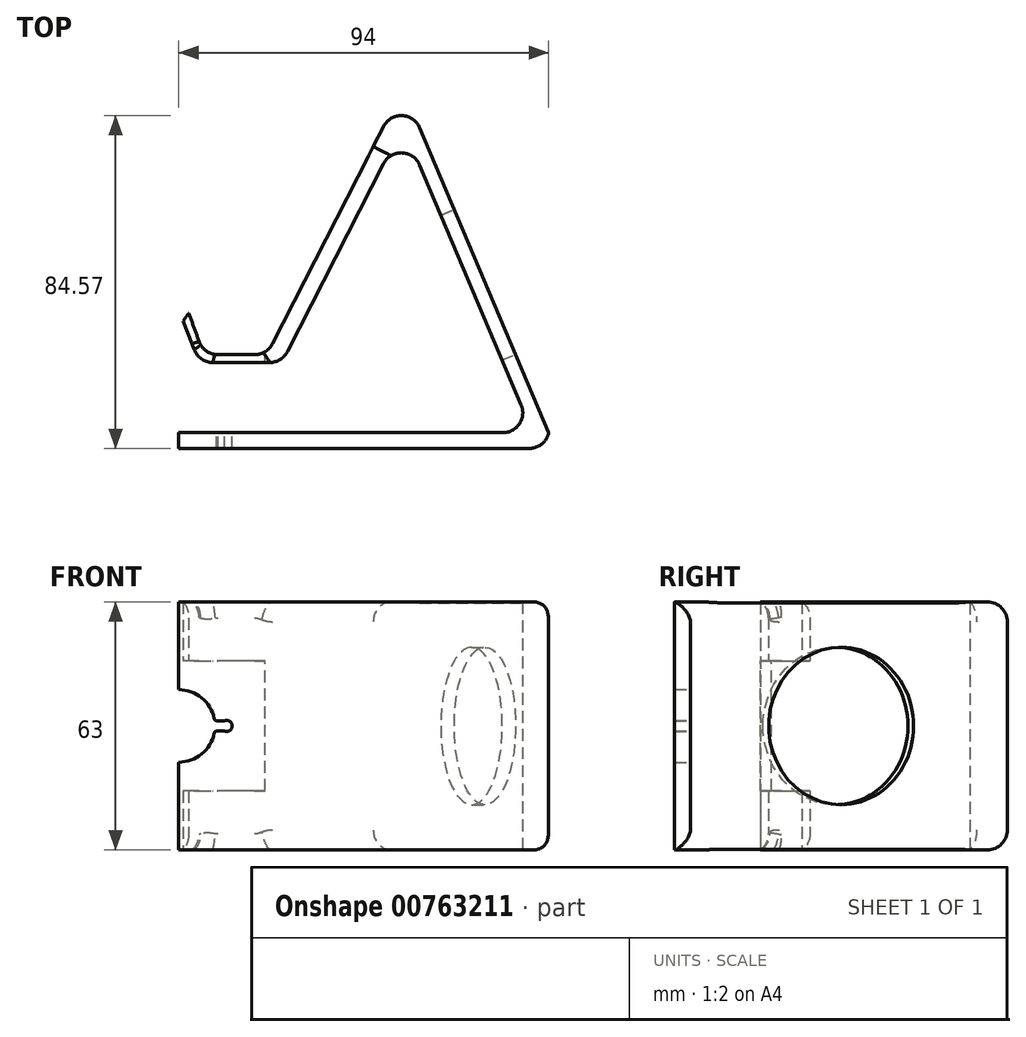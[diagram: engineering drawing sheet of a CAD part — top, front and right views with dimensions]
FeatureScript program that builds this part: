
annotation { "Feature Type Name" : "Feature", "Feature Type Description" : "" }
export const myFeature = defineFeature(function(context is Context, id is Id, definition is map)
    precondition{}
    {
        {
            var Q0;
            Q0=qCreatedBy(makeId("Top.planeOp"),FACE);
            var sketch = newSketch(context, id + "F0", { "sketchPlane" : qUnion([Q0])});
            skLineSegment(sketch, "E0", {"start": v(0, 43.75) * mm, "end": v(0, -43.75) * mm, "construction": true});
            skLineSegment(sketch, "E1", {"start": v(-37, -43.75) * mm, "end": v(33, -43.75) * mm});
            skPoint(sketch, "E2", {"position": v(0, -43.75) * mm});
            skLineSegment(sketch, "E3", {"start": v(0, 43.75) * mm, "end": v(37, -43.75) * mm});
            skLineSegment(sketch, "E4", {"start": v(0, 43.75) * mm, "end": v(-34.6, -23.92) * mm});
            skLineSegment(sketch, "E5.top", {"start": v(-37, -47.75) * mm, "end": v(37, -47.75) * mm});
            skLineSegment(sketch, "E5.right", {"start": v(37, -43.75) * mm, "end": v(37, -47.75) * mm});
            skLineSegment(sketch, "E6", {"start": v(33, -43.75) * mm, "end": v(0, 34.3) * mm});
            skLineSegment(sketch, "E7", {"start": v(0, 34.3) * mm, "end": v(-30.78, -25.92) * mm});
            skLineSegment(sketch, "E8", {"start": v(-30.78, -25.92) * mm, "end": v(-51.78, -25.92) * mm});
            skLineSegment(sketch, "E9", {"start": v(-51.78, -25.92) * mm, "end": v(-55.84, -15.4) * mm});
            skLineSegment(sketch, "E10", {"start": v(-34.6, -23.92) * mm, "end": v(-50.6, -23.92) * mm});
            skLineSegment(sketch, "E11", {"start": v(-50.6, -23.92) * mm, "end": v(-54.45, -13.32) * mm});
            skLineSegment(sketch, "E12", {"start": v(-54.45, -13.32) * mm, "end": v(-55.84, -15.4) * mm});
            skLineSegment(sketch, "E13", {"start": v(-55.84, -15.4) * mm, "end": v(0, -15.4) * mm, "construction": true});
            skLineSegment(sketch, "E14", {"start": v(-55.84, -15.4) * mm, "end": v(-55.84, 0) * mm, "construction": true});
            skLineSegment(sketch, "E15.bottom", {"start": v(-37, -47.75) * mm, "end": v(-57, -47.75) * mm});
            skLineSegment(sketch, "E15.top", {"start": v(-37, -43.75) * mm, "end": v(-57, -43.75) * mm});
            skLineSegment(sketch, "E15.right", {"start": v(-57, -47.75) * mm, "end": v(-57, -43.75) * mm});
            skSolve(sketch);
        }
        {
            var Q0;
            Q0 = qSketchRegion(id + "F0", true);
            extrude(context, id + "F1", {"entities" : qUnion([Q0]), "depth" : 63 * mm, "offsetDistance" : 25.4 * mm});
        }
        {
            var Q0;
            Q0=qCreatedBy(makeId("Right.planeOp"),FACE);
            cPlane(context, id + "F2", {"entities" : qUnion([Q0]), "cplaneType" : CPlaneType.OFFSET, "offset" : 56 * mm, "oppositeDirection" : true, "width" : 152.4 * mm, "height" : 152.4 * mm});
        }
        {
            var Q0;
            Q0=qCreatedBy(id+"F2.planeOp",FACE);
            var sketch = newSketch(context, id + "F3", { "sketchPlane" : qUnion([Q0])});
            skLineSegment(sketch, "E16", {"start": v(0, 0) * mm, "end": v(-30, 0) * mm, "construction": true});
            skLineSegment(sketch, "E17", {"start": v(-30, 0) * mm, "end": v(-30, 63) * mm, "construction": true});
            skPoint(sketch, "E18", {"position": v(-30, 15) * mm});
            skPoint(sketch, "E19", {"position": v(-30, 48) * mm});
            skLineSegment(sketch, "E20.bottom", {"start": v(-30, 15) * mm, "end": v(-6.4, 15) * mm});
            skLineSegment(sketch, "E20.top", {"start": v(-30, 48) * mm, "end": v(-6.4, 48) * mm});
            skLineSegment(sketch, "E20.left", {"start": v(-30, 15) * mm, "end": v(-30, 48) * mm});
            skLineSegment(sketch, "E20.right", {"start": v(-6.4, 15) * mm, "end": v(-6.4, 48) * mm});
            skSolve(sketch);
        }
        {
            var Q0;
            Q0=makeQuery(id+"F3.imprint","IMPRINT",FACE,{"disambiguationData":[TD([[makeQuery(id+"F3.imprint","IMPRINT",EDGE,{"derivedFrom":sQuery(id+"F3.wireOp",EDGE,"E20.bottom")}),1.0]])]});
            extrude(context, id + "F4", {"entities" : qUnion([Q0]), "operationType" : NewBodyOperationType.REMOVE, "depth" : 21 * mm, "offsetDistance" : 25.4 * mm});
        }
        {
            var Q0;
            Q0=makeQuery(id+"F1.opExtrude","SWEPT_EDGE",EDGE,{"disambiguationData":[OSD([sQuery(id+"F0.wireOp",EDGE,"E3"),sQuery(id+"F0.wireOp",EDGE,"E4")])]});
            var Q1;
            Q1=makeQuery(id+"F1.opExtrude","SWEPT_EDGE",EDGE,{"disambiguationData":[OSD([sQuery(id+"F0.wireOp",EDGE,"E6"),sQuery(id+"F0.wireOp",EDGE,"E7")])]});
            var Q2;
            Q2=makeQuery(id+"F1.opExtrude","SWEPT_EDGE",EDGE,{"disambiguationData":[OSD([sQuery(id+"F0.wireOp",EDGE,"E1"),sQuery(id+"F0.wireOp",EDGE,"E6")])]});
            var Q3;
            {var subQ0=sQuery(id+"F0.wireOp",EDGE,"E9");var subQ1=sQuery(id+"F0.wireOp",EDGE,"E8");Q3=makeQuery(id+"F4.boolean.opBoolean","SPLIT",EDGE,{"disambiguationData":[TD([makeQuery(id+"F4.opExtrude","SWEPT_FACE",FACE,{"disambiguationData":[OSD([sQuery(id+"F3.wireOp",EDGE,"E20.top")])]})])],"derivedFrom":makeQuery(id+"F1.opExtrude","SWEPT_EDGE",EDGE,{"disambiguationData":[OSD([subQ1,subQ0])]})});}
            var Q4;
            {var subQ0=sQuery(id+"F0.wireOp",EDGE,"E9");var subQ1=sQuery(id+"F0.wireOp",EDGE,"E8");Q4=makeQuery(id+"F4.boolean.opBoolean","SPLIT",EDGE,{"disambiguationData":[TD([makeQuery(id+"F4.opExtrude","SWEPT_FACE",FACE,{"disambiguationData":[OSD([sQuery(id+"F3.wireOp",EDGE,"E20.bottom")])]})])],"derivedFrom":makeQuery(id+"F1.opExtrude","SWEPT_EDGE",EDGE,{"disambiguationData":[OSD([subQ1,subQ0])]})});}
            var Q5;
            {var subQ0=sQuery(id+"F0.wireOp",EDGE,"E11");var subQ1=sQuery(id+"F0.wireOp",EDGE,"E10");Q5=makeQuery(id+"F4.boolean.opBoolean","SPLIT",EDGE,{"disambiguationData":[TD([makeQuery(id+"F4.opExtrude","SWEPT_FACE",FACE,{"disambiguationData":[OSD([sQuery(id+"F3.wireOp",EDGE,"E20.top")])]})])],"derivedFrom":makeQuery(id+"F1.opExtrude","SWEPT_EDGE",EDGE,{"disambiguationData":[OSD([subQ1,subQ0])]})});}
            var Q6;
            {var subQ0=sQuery(id+"F0.wireOp",EDGE,"E11");var subQ1=sQuery(id+"F0.wireOp",EDGE,"E10");Q6=makeQuery(id+"F4.boolean.opBoolean","SPLIT",EDGE,{"disambiguationData":[TD([makeQuery(id+"F4.opExtrude","SWEPT_FACE",FACE,{"disambiguationData":[OSD([sQuery(id+"F3.wireOp",EDGE,"E20.bottom")])]})])],"derivedFrom":makeQuery(id+"F1.opExtrude","SWEPT_EDGE",EDGE,{"disambiguationData":[OSD([subQ1,subQ0])]})});}
            var Q7;
            Q7=makeQuery(id+"F1.opExtrude","SWEPT_EDGE",EDGE,{"disambiguationData":[OSD([sQuery(id+"F0.wireOp",EDGE,"E7"),sQuery(id+"F0.wireOp",EDGE,"E8")])]});
            var Q8;
            Q8=makeQuery(id+"F1.opExtrude","SWEPT_EDGE",EDGE,{"disambiguationData":[OSD([sQuery(id+"F0.wireOp",EDGE,"E4"),sQuery(id+"F0.wireOp",EDGE,"E10")])]});
            var Q9;
            Q9=makeQuery(id+"F1.opExtrude","SWEPT_EDGE",EDGE,{"disambiguationData":[OSD([sQuery(id+"F0.wireOp",EDGE,"E5.top"),sQuery(id+"F0.wireOp",EDGE,"E5.right")])]});
            fillet(context, id + "F5", {"entities" : qUnion([Q0, Q1, Q2, Q3, Q4, Q5, Q6, Q7, Q8, Q9]), "tangentPropagation" : true, "radius" : 5.08 * mm, "defaultsChanged" : false, "vertexSettings" : [], "allowEdgeOverflow" : false});
        }
        {
            var Q0;
            Q0=makeQuery(id+"F1.opExtrude","SWEPT_FACE",FACE,{"disambiguationData":[OSD([sQuery(id+"F0.wireOp",EDGE,"E3")])]});
            var sketch = newSketch(context, id + "F6", { "sketchPlane" : qUnion([Q0])});
            skCircle(sketch, "E21", {"center": v(-13.12, 31.5) * mm, "radius": 20 * mm});
            skSolve(sketch);
        }
        {
            var Q0;
            Q0=makeQuery(id+"F6.imprint","IMPRINT",FACE,{"disambiguationData":[TD([[makeQuery(id+"F6.imprint","IMPRINT",EDGE,{"derivedFrom":sQuery(id+"F6.wireOp",EDGE,"E21")}),1.0]])]});
            extrude(context, id + "F7", {"entities" : qUnion([Q0]), "operationType" : NewBodyOperationType.REMOVE, "oppositeDirection" : true, "depth" : 25.4 * mm, "offsetDistance" : 25.4 * mm});
        }
        {
            var Q0;
            Q0=makeQuery(id+"F1.opExtrude","SWEPT_FACE",FACE,{"disambiguationData":[OSD([sQuery(id+"F0.wireOp",EDGE,"E1"),sQuery(id+"F0.wireOp",EDGE,"E15.top")])]});
            var sketch = newSketch(context, id + "F8", { "sketchPlane" : qUnion([Q0])});
            skArc(sketch, "E22", {"start": v(57, 40.72) * mm, "mid": v(51.17, 38.64) * mm, "end": v(47.97, 33.33) * mm});
            skLineSegment(sketch, "E23", {"start": v(57, 22.28) * mm, "end": v(57, 40.72) * mm});
            skArc(sketch, "E24", {"start": v(45.3, 32.83) * mm, "mid": v(43.4, 31.5) * mm, "end": v(45.3, 30.18) * mm});
            skLineSegment(sketch, "E25", {"start": v(45.3, 30.18) * mm, "end": v(47.02, 30.18) * mm});
            skLineSegment(sketch, "E26", {"start": v(45.3, 32.83) * mm, "end": v(47.02, 32.83) * mm});
            skArc(sketch, "E27.trimOffspring", {"start": v(47.97, 29.67) * mm, "mid": v(51.17, 24.36) * mm, "end": v(57, 22.28) * mm});
            skPoint(sketch, "E28.visualSharp", {"position": v(47.88, 30.18) * mm});
            skArc(sketch, "E28.filletArc", {"start": v(47.97, 29.67) * mm, "mid": v(47.75, 30.03) * mm, "end": v(47.35, 30.18) * mm});
            skPoint(sketch, "E29.visualSharp", {"position": v(47.88, 32.83) * mm});
            skArc(sketch, "E29.filletArc", {"start": v(47.35, 32.83) * mm, "mid": v(47.75, 32.97) * mm, "end": v(47.97, 33.33) * mm});
            skLineSegment(sketch, "E30", {"start": v(44.8, 31.5) * mm, "end": v(57, 31.5) * mm, "construction": true});
            skLineSegment(sketch, "E31", {"start": v(47.35, 32.83) * mm, "end": v(47.35, 30.18) * mm, "construction": true});
            skPoint(sketch, "E32", {"position": v(47.35, 31.5) * mm});
            skLineSegment(sketch, "E33", {"start": v(57, 31.5) * mm, "end": v(57, 40.72) * mm, "construction": true});
            skLineSegment(sketch, "E34", {"start": v(57, 22.28) * mm, "end": v(57, 31.5) * mm, "construction": true});
            skArc(sketch, "E35", {"start": v(47.02, 32.83) * mm, "mid": v(47.18, 32.77) * mm, "end": v(47.35, 32.83) * mm});
            skArc(sketch, "E36.MirrorCS", {"start": v(47.02, 30.18) * mm, "mid": v(47.18, 30.23) * mm, "end": v(47.35, 30.18) * mm});
            skSolve(sketch);
        }
        {
            var Q0;
            Q0=makeQuery(id+"F8.imprint","IMPRINT",FACE,{"disambiguationData":[TD([[makeQuery(id+"F8.imprint","IMPRINT",EDGE,{"derivedFrom":sQuery(id+"F8.wireOp",EDGE,"E22")}),1.0]])]});
            extrude(context, id + "F9", {"entities" : qUnion([Q0]), "operationType" : NewBodyOperationType.REMOVE, "oppositeDirection" : true, "depth" : 25.4 * mm, "offsetDistance" : 25.4 * mm});
        }
        {
            var Q0;
            Q0=makeQuery(id+"F1.opExtrude","CAP_EDGE",EDGE,{"disambiguationData":[OSD([sQuery(id+"F0.wireOp",EDGE,"E3")])],"isStart":false});
            var Q1;
            Q1=makeQuery(id+"F1.opExtrude","CAP_EDGE",EDGE,{"disambiguationData":[OSD([sQuery(id+"F0.wireOp",EDGE,"E3")])],"isStart":true});
            fillet(context, id + "F10", {"entities" : qUnion([Q0, Q1]), "tangentPropagation" : true, "radius" : 5.08 * mm, "defaultsChanged" : false, "vertexSettings" : [], "allowEdgeOverflow" : false});
        }
    });
